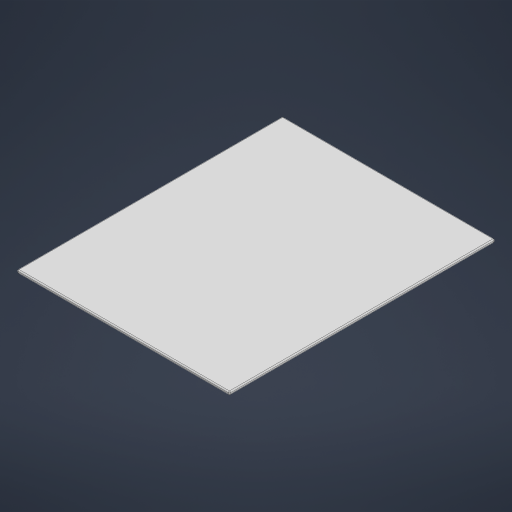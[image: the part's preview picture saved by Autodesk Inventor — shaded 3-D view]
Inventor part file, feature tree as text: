
AUTODESK INVENTOR PART (.ipt)
format: ipt  version: 2023 (Build 270158000, 158)  size: 193,024 bytes
history: native  units: mm
features: extrude x1, fillet x1, other x1
ambient origin geometry x8: Origin, YZ Plane, XZ Plane, XY Plane, X Axis, Y Axis, Z Axis, Center Point
bodies: Solid1 (feature_tree)
feature tree (3):
  extrude  "cover"  Depth=200.0mm
  fillet  "Fillet1"  Radius=250.0mm
  other  "page_lines"
